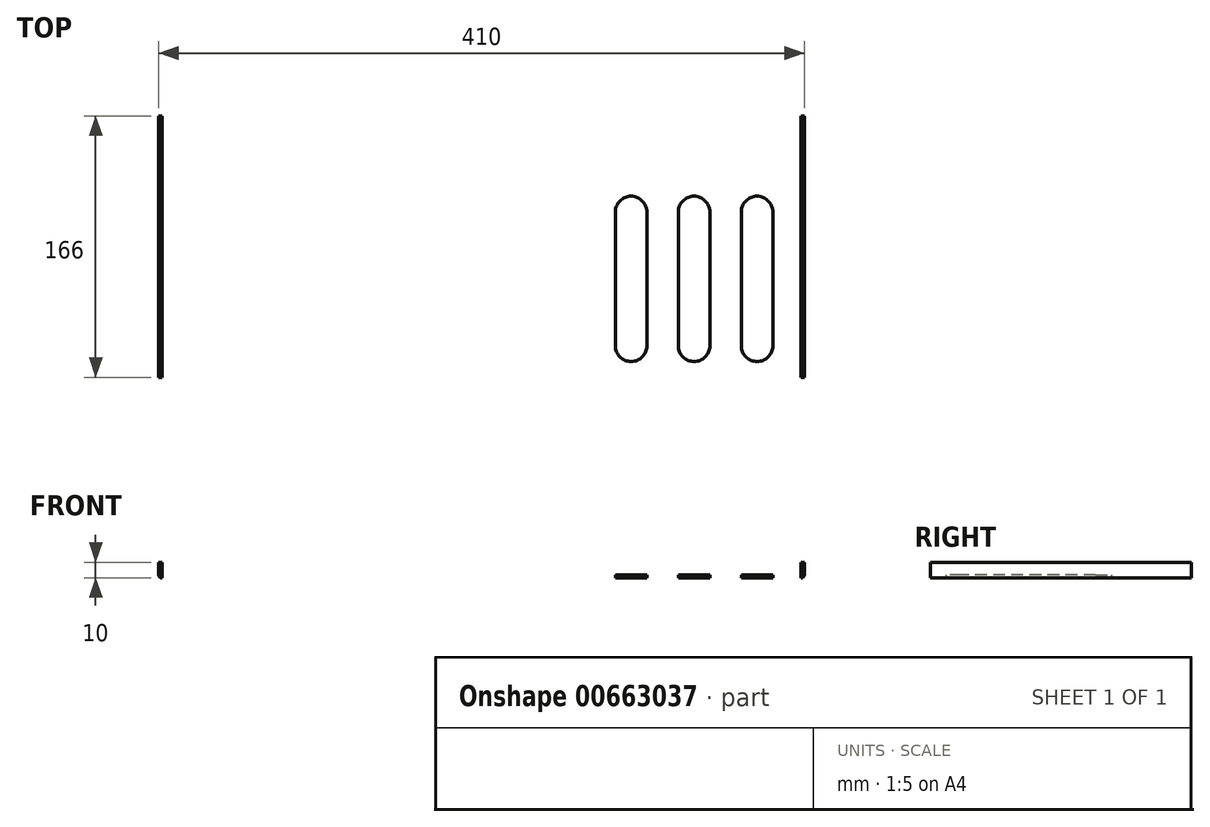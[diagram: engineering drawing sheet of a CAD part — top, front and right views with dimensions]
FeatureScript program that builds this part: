
annotation { "Feature Type Name" : "Feature", "Feature Type Description" : "" }
export const myFeature = defineFeature(function(context is Context, id is Id, definition is map)
    precondition{}
    {
        {
            var Q0;
            Q0=qCreatedBy(makeId("Front.planeOp"),FACE);
            var sketch = newSketch(context, id + "F0", { "sketchPlane" : qUnion([Q0])});
            skLineSegment(sketch, "E0", {"start": v(0, 0) * mm, "end": v(0, 8) * mm});
            skLineSegment(sketch, "E1", {"start": v(2, 10) * mm, "end": v(408, 10) * mm});
            skLineSegment(sketch, "E2", {"start": v(410, 8) * mm, "end": v(410, 0) * mm});
            skLineSegment(sketch, "E3.0", {"start": v(408, 8) * mm, "end": v(408, 0) * mm});
            skLineSegment(sketch, "E3.1", {"start": v(2, 8) * mm, "end": v(408, 8) * mm});
            skLineSegment(sketch, "E3.2", {"start": v(2, 0) * mm, "end": v(2, 8) * mm});
            skLineSegment(sketch, "E4", {"start": v(408, 0) * mm, "end": v(410, 0) * mm});
            skLineSegment(sketch, "E5", {"start": v(0, 0) * mm, "end": v(2, 0) * mm});
            skPoint(sketch, "E6.visualSharp", {"position": v(410, 10) * mm});
            skArc(sketch, "E6.filletArc", {"start": v(410, 8) * mm, "mid": v(409.41, 9.41) * mm, "end": v(408, 10) * mm});
            skPoint(sketch, "E7.visualSharp", {"position": v(0, 10) * mm});
            skArc(sketch, "E7.filletArc", {"start": v(2, 10) * mm, "mid": v(0.59, 9.41) * mm, "end": v(0, 8) * mm});
            skArc(sketch, "E8.MirrorCS", {"start": v(2, 10) * mm, "mid": v(0.59, 10.59) * mm, "end": v(0, 12) * mm});
            skLineSegment(sketch, "E9.MirrorCS", {"start": v(0, 20) * mm, "end": v(0, 12) * mm});
            skLineSegment(sketch, "E10.MirrorCS", {"start": v(2, 20) * mm, "end": v(2, 12) * mm});
            skLineSegment(sketch, "E11.MirrorCS", {"start": v(2, 12) * mm, "end": v(408, 12) * mm});
            skLineSegment(sketch, "E12.MirrorCS", {"start": v(408, 12) * mm, "end": v(408, 20) * mm});
            skLineSegment(sketch, "E13.MirrorCS", {"start": v(408, 20) * mm, "end": v(410, 20) * mm});
            skLineSegment(sketch, "E14.MirrorCS", {"start": v(410, 12) * mm, "end": v(410, 20) * mm});
            skArc(sketch, "E15.MirrorCS", {"start": v(410, 12) * mm, "mid": v(409.41, 10.59) * mm, "end": v(408, 10) * mm});
            skLineSegment(sketch, "E16.MirrorCS", {"start": v(0, 20) * mm, "end": v(2, 20) * mm});
            skSolve(sketch);
        }
        {
            var Q0;
            Q0=makeQuery(id+"F0.imprint","IMPRINT",FACE,{"disambiguationData":[TD([[makeQuery(id+"F0.imprint","IMPRINT",EDGE,{"derivedFrom":sQuery(id+"F0.wireOp",EDGE,"E1")}),1.0]])]});
            extrude(context, id + "F1", {"entities" : qUnion([Q0]), "oppositeDirection" : true, "depth" : 166 * mm, "offsetDistance" : 25 * mm});
        }
        {
            var Q0;
            Q0=makeQuery(id+"F1.opExtrude","SWEPT_FACE",FACE,{"disambiguationData":[OSD([sQuery(id+"F0.wireOp",EDGE,"E1")])]});
            var sketch = newSketch(context, id + "F2", { "sketchPlane" : qUnion([Q0])});
            skPoint(sketch, "E17", {"position": v(300, -62.5) * mm});
            skPoint(sketch, "E18", {"position": v(340, -62.5) * mm});
            skPoint(sketch, "E19", {"position": v(380, -62.5) * mm});
            skPoint(sketch, "E20", {"position": v(300, -166) * mm});
            skPoint(sketch, "E21", {"position": v(340, -166) * mm});
            skPoint(sketch, "E22", {"position": v(380, -166) * mm});
            skLineSegment(sketch, "E23", {"start": v(300, -20) * mm, "end": v(300, -105) * mm});
            skArc(sketch, "E24.0.startCap", {"start": v(290, -20) * mm, "mid": v(300, -10) * mm, "end": v(310, -20) * mm});
            skArc(sketch, "E24.0.endCap", {"start": v(310, -105) * mm, "mid": v(300, -115) * mm, "end": v(290, -105) * mm});
            skLineSegment(sketch, "E24.0.left", {"start": v(310, -20) * mm, "end": v(310, -105) * mm});
            skLineSegment(sketch, "E24.0.right", {"start": v(290, -20) * mm, "end": v(290, -105) * mm});
            skLineSegment(sketch, "E25", {"start": v(340, -20) * mm, "end": v(340, -105) * mm});
            skLineSegment(sketch, "E26", {"start": v(380, -20) * mm, "end": v(380, -105) * mm});
            skArc(sketch, "E27.0.startCap", {"start": v(330, -20) * mm, "mid": v(340, -10) * mm, "end": v(350, -20) * mm});
            skArc(sketch, "E27.0.endCap", {"start": v(350, -105) * mm, "mid": v(340, -115) * mm, "end": v(330, -105) * mm});
            skLineSegment(sketch, "E27.0.left", {"start": v(350, -20) * mm, "end": v(350, -105) * mm});
            skLineSegment(sketch, "E27.0.right", {"start": v(330, -20) * mm, "end": v(330, -105) * mm});
            skArc(sketch, "E27.1.startCap", {"start": v(370, -20) * mm, "mid": v(380, -10) * mm, "end": v(390, -20) * mm});
            skArc(sketch, "E27.1.endCap", {"start": v(390, -105) * mm, "mid": v(380, -115) * mm, "end": v(370, -105) * mm});
            skLineSegment(sketch, "E27.1.left", {"start": v(390, -20) * mm, "end": v(390, -105) * mm});
            skLineSegment(sketch, "E27.1.right", {"start": v(370, -20) * mm, "end": v(370, -105) * mm});
            skSolve(sketch);
        }
        {
            var Q0;
            Q0=makeQuery(id+"F2.imprint","IMPRINT",FACE,{"disambiguationData":[TD([[makeQuery(id+"F2.imprint","IMPRINT",EDGE,{"derivedFrom":sQuery(id+"F2.wireOp",EDGE,"E24.0.startCap")}),-1.0]])]});
            var Q1;
            Q1=makeQuery(id+"F2.imprint","IMPRINT",FACE,{"disambiguationData":[TD([[makeQuery(id+"F2.imprint","IMPRINT",EDGE,{"derivedFrom":sQuery(id+"F2.wireOp",EDGE,"E27.0.startCap")}),-1.0]])]});
            var Q2;
            Q2=makeQuery(id+"F2.imprint","IMPRINT",FACE,{"disambiguationData":[TD([[makeQuery(id+"F2.imprint","IMPRINT",EDGE,{"derivedFrom":sQuery(id+"F2.wireOp",EDGE,"E27.1.startCap")}),-1.0]])]});
            extrude(context, id + "F3", {"entities" : qUnion([Q0, Q1, Q2]), "operationType" : NewBodyOperationType.REMOVE, "endBound" : BoundingType.UP_TO_NEXT, "oppositeDirection" : true, "depth" : 25 * mm, "offsetDistance" : 25 * mm});
        }
        {
            var Q0;
            Q0=sQuery(id+"F2.wireOp",VERTEX,"E20");
            var Q1;
            Q1=sQuery(id+"F2.wireOp",VERTEX,"E21");
            var Q2;
            Q2=sQuery(id+"F2.wireOp",VERTEX,"E22");
            var Q3;
            Q3=makeQuery(id+"F1.opExtrude","SWEPT_BODY",BODY,{"disambiguationData":[OSD([sQuery(id+"F0.wireOp",EDGE,"E0"),sQuery(id+"F0.wireOp",EDGE,"E1"),sQuery(id+"F0.wireOp",EDGE,"E2"),sQuery(id+"F0.wireOp",EDGE,"E3.0"),sQuery(id+"F0.wireOp",EDGE,"E3.1"),sQuery(id+"F0.wireOp",EDGE,"E3.2"),sQuery(id+"F0.wireOp",EDGE,"E4"),sQuery(id+"F0.wireOp",EDGE,"E5"),sQuery(id+"F0.wireOp",EDGE,"E6.filletArc"),sQuery(id+"F0.wireOp",EDGE,"E7.filletArc")])]});
            hole(context, id + "F4", {"style" : HoleStyle.SIMPLE, "endStyle" : HoleEndStyle.BLIND, "holeDiameter" : 20 * mm, "majorDiameter" : 5 * mm, "holeDepth" : 5 * mm, "isTappedThrough" : true, "tappedDepth" : 12 * mm, "tapClearance" : 3, "locations" : qUnion([Q0, Q1, Q2]), "scope" : qUnion([Q3])});
        }
    });
